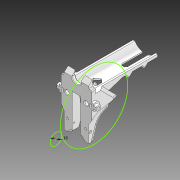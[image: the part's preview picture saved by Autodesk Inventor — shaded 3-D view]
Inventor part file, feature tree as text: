
AUTODESK INVENTOR PART (.ipt)
format: ipt  version: 2020 (Build 240168000, 168)  size: 549,888 bytes
history: native  units: in
note: dims shown in document units (in); Inventor stores cm internally (conversion verified against a paired STEP export)
features: extrude x11, sketch x11, projected_geometry x3, plane x1, mirror x1, imported_body x1
ambient origin geometry x8: Origin, YZ Plane, XZ Plane, XY Plane, X Axis, Y Axis, Z Axis, Center Point
bodies: Solid1 (feature_tree)
feature tree (28):
  extrude  "Extrusion1"  Depth=0.315in
  extrude  "Extrusion2"  Depth=0.2756in TaperAngle=0.0deg
  extrude  "Extrusion9"  Depth=0.3937in TaperAngle=0.0deg
  extrude  "Extrusion10"  Depth=0.1181in TaperAngle=0.0deg
  plane  "Work Plane1"
  extrude  "Extrusion11"  Depth=0.0787in
  mirror  "Mirror1"
  extrude  "Extrusion3"  Depth=0.3937in TaperAngle=0.0deg
  extrude  "Extrusion7"  Depth=0.0787in
  extrude  "Extrusion4"  Depth=0.1378in
  extrude  "Extrusion5"  Depth=0.0787in
  extrude  "Extrusion6"  Depth=0.2165in
  extrude  "Extrusion8"  Depth=0.1024in TaperAngle=0.0deg
  sketch  "Sketch1"  dims[d0=0.3937in d1=0.0in d2=0.315in]
  sketch  "Sketch2"  dims[d3=0.1378in d4=0.2756in d5=0.0in]
  sketch  "Sketch3"  dims[d6=0.3937in d7=0.0in d8=0.3937in d9=0.0in]
  projected_geometry  "Projected Loop1"
  sketch  "Sketch4"  dims[d10=0.1181in d11=0.0in d12=0.1181in d13=0.0in]
  sketch  "Sketch5"  dims[d14=1.5866in d15=0.0787in]
  projected_geometry  "Projected Loop2"
  sketch  "Sketch6"  dims[d16=0.3937in d17=0.1181in d18=0.0in]
  projected_geometry  "Projected Loop3"
  sketch  "Sketch7"  dims[d19=0.0in d20=0.0in d21=0.0787in]
  sketch  "Sketch8"  dims[d22=0.1181in d23=0.0in d24=0.1378in]
  sketch  "Sketch9"  dims[d25=0.4724in d26=0.0in d27=0.0787in]
  sketch  "Sketch10"  dims[d28=0.2165in d29=0.2165in]
  sketch  "Sketch11"  dims[d30=0.1969in d31=0.1024in d32=0.0in]
  imported_body  "Base1"
